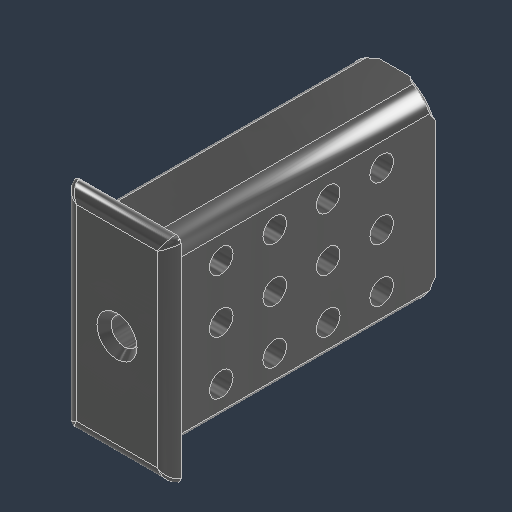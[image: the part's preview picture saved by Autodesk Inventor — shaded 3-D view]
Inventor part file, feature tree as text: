
AUTODESK INVENTOR PART (.ipt)
format: ipt  version: 2024.3 (Build 283343000, 343)  size: 309,760 bytes
history: native  units: in
note: dims shown in document units (in); Inventor stores cm internally (conversion verified against a paired STEP export)
features: sketch x5, extrude x3, fillet x2, hole x2, chamfer x1, pattern_linear x1
ambient origin geometry x8: Origin, YZ Plane, XZ Plane, XY Plane, X Axis, Y Axis, Z Axis, Center Point
bodies: Solid1 (feature_tree)
feature tree (14):
  extrude  "Extrusion1"  Depth=2.5in TaperAngle=0.0deg
  extrude  "Extrusion2"  Depth=2.0in
  fillet  "Fillet1"  Radius=0.1in
  fillet  "Fillet2"  Radius=0.125in
  hole  "Hole1"  [1 undecoded]
  hole  "Hole2"  [1 undecoded]
  chamfer  "Chamfer1"  Distance=1.0in
  pattern_linear  "Rectangular Pattern1"  Count1=4 Spacing1=0.5in
  extrude  "Extrusion3"  Depth=0.75in
  sketch  "Sketch1"  dims[d0=0.005in d1=2.5in d2=0.0in]
  sketch  "Sketch2"  dims[d3=1.0in d4=2.0in d5=0.1in d6=0.0in d7=0.125in]
  sketch  "Sketch3"  dims[d8=0.05in]
  sketch  "Sketch4"  dims[d9=0.25in d10=0.75in d11=0.375in d12=0.25in d13=0.5635in d14=1.0in d15=0.8108in]
  sketch  "Sketch5"  dims[d16=0.221in d17=0.75in d18=0.385in d19=0.25in d20=0.5635in d21=1.0in d22=0.8108in d23=0.05in d24=0.125in d25=45.0deg d26=0.5in d27=1.0in d28=1.5748in d30=0.5in d31=1.0in d32=2.0in d33=0.125in d34=1.0in d35=0.0in]
note: 2 required parameter values undecoded (feature->parameter linkage not recoverable at this tier; creation-order binding heuristic only, values carry confidence <= 0.55)
